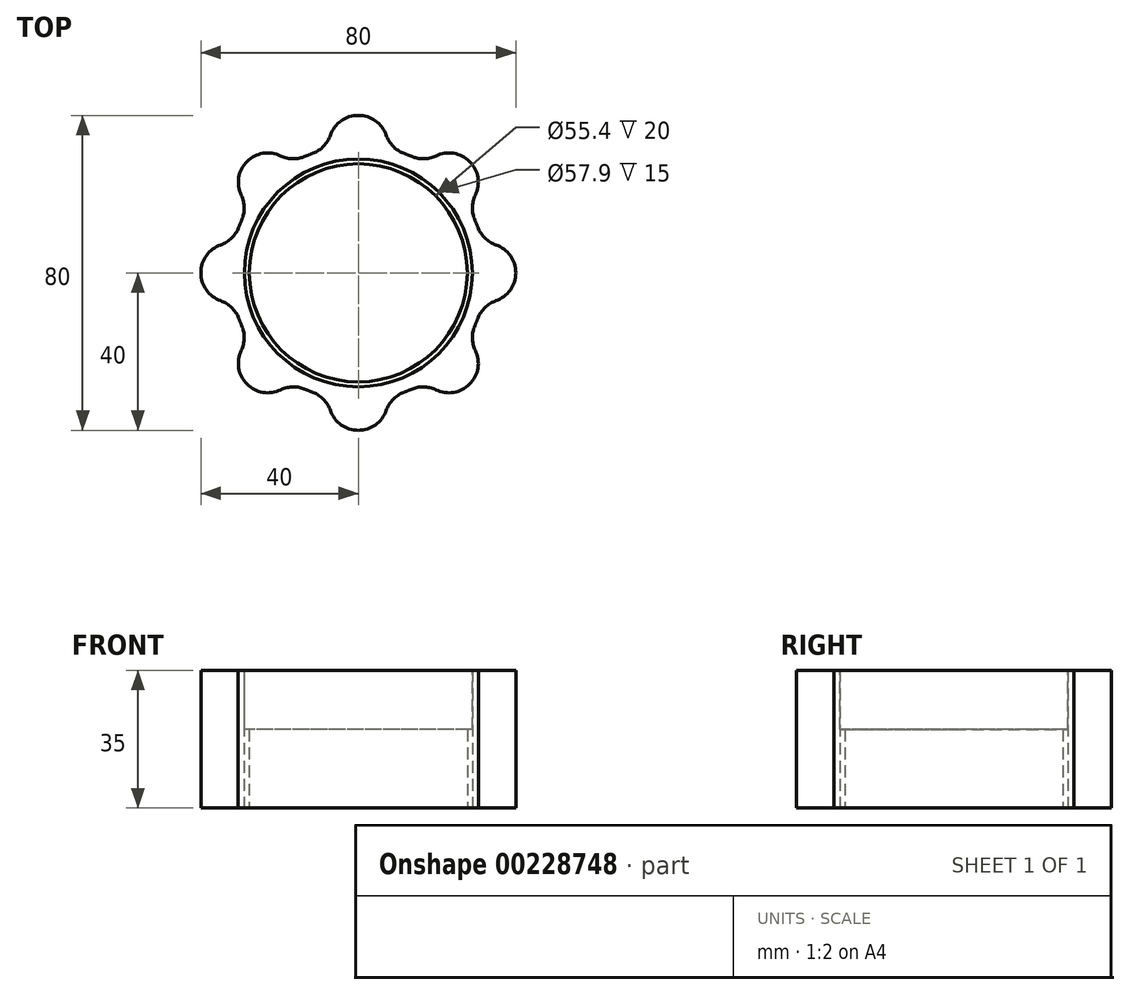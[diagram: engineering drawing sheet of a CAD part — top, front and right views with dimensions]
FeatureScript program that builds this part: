
annotation { "Feature Type Name" : "Feature", "Feature Type Description" : "" }
export const myFeature = defineFeature(function(context is Context, id is Id, definition is map)
    precondition{}
    {
        {
            var Q0;
            Q0=qCreatedBy(makeId("Top.planeOp"),FACE);
            var sketch = newSketch(context, id + "F0", { "sketchPlane" : qUnion([Q0])});
            skCircle(sketch, "E0", {"center": v(0, 0) * mm, "radius": 27.7 * mm});
            skCircle(sketch, "E1", {"center": v(0, 0) * mm, "radius": 40 * mm, "construction": true});
            skArc(sketch, "E2", {"start": v(-11.52, 30.4) * mm, "mid": v(-12.44, 30.03) * mm, "end": v(-13.35, 29.63) * mm});
            skArc(sketch, "E3", {"start": v(7.09, 34.95) * mm, "mid": v(0, 40) * mm, "end": v(-7.09, 34.95) * mm});
            skPoint(sketch, "E4.visualSharp", {"position": v(-7.45, 31.63) * mm});
            skArc(sketch, "E4.filletArc", {"start": v(-11.52, 30.4) * mm, "mid": v(-8.8, 32.18) * mm, "end": v(-7.09, 34.95) * mm});
            skPoint(sketch, "E5.visualSharp", {"position": v(7.45, 31.63) * mm});
            skArc(sketch, "E5.filletArc", {"start": v(7.09, 34.95) * mm, "mid": v(8.8, 32.18) * mm, "end": v(11.52, 30.4) * mm});
            skArc(sketch, "E6.1.0", {"start": v(-29.63, 13.35) * mm, "mid": v(-28.97, 16.53) * mm, "end": v(-29.73, 19.7) * mm});
            skArc(sketch, "E6.1.1", {"start": v(-19.7, 29.73) * mm, "mid": v(-28.28, 28.28) * mm, "end": v(-29.73, 19.7) * mm});
            skArc(sketch, "E6.1.2", {"start": v(-19.7, 29.73) * mm, "mid": v(-16.53, 28.97) * mm, "end": v(-13.35, 29.63) * mm});
            skArc(sketch, "E6.2.0", {"start": v(-30.4, -11.52) * mm, "mid": v(-32.18, -8.8) * mm, "end": v(-34.95, -7.09) * mm});
            skArc(sketch, "E6.2.1", {"start": v(-34.95, 7.09) * mm, "mid": v(-40, 0) * mm, "end": v(-34.95, -7.09) * mm});
            skArc(sketch, "E6.2.2", {"start": v(-34.95, 7.09) * mm, "mid": v(-32.18, 8.8) * mm, "end": v(-30.4, 11.52) * mm});
            skArc(sketch, "E6.3.0", {"start": v(-13.35, -29.63) * mm, "mid": v(-16.53, -28.97) * mm, "end": v(-19.7, -29.73) * mm});
            skArc(sketch, "E6.3.1", {"start": v(-29.73, -19.7) * mm, "mid": v(-28.28, -28.28) * mm, "end": v(-19.7, -29.73) * mm});
            skArc(sketch, "E6.3.2", {"start": v(-29.73, -19.7) * mm, "mid": v(-28.97, -16.53) * mm, "end": v(-29.63, -13.35) * mm});
            skArc(sketch, "E6.4.0", {"start": v(11.52, -30.4) * mm, "mid": v(8.8, -32.18) * mm, "end": v(7.09, -34.95) * mm});
            skArc(sketch, "E6.4.1", {"start": v(-7.09, -34.95) * mm, "mid": v(0, -40) * mm, "end": v(7.09, -34.95) * mm});
            skArc(sketch, "E6.4.2", {"start": v(-7.09, -34.95) * mm, "mid": v(-8.8, -32.18) * mm, "end": v(-11.52, -30.4) * mm});
            skArc(sketch, "E6.5.0", {"start": v(29.63, -13.35) * mm, "mid": v(28.97, -16.53) * mm, "end": v(29.73, -19.7) * mm});
            skArc(sketch, "E6.5.1", {"start": v(19.7, -29.73) * mm, "mid": v(28.28, -28.28) * mm, "end": v(29.73, -19.7) * mm});
            skArc(sketch, "E6.5.2", {"start": v(19.7, -29.73) * mm, "mid": v(16.53, -28.97) * mm, "end": v(13.35, -29.63) * mm});
            skArc(sketch, "E6.6.0", {"start": v(30.4, 11.52) * mm, "mid": v(32.18, 8.8) * mm, "end": v(34.95, 7.09) * mm});
            skArc(sketch, "E6.6.1", {"start": v(34.95, -7.09) * mm, "mid": v(40, 0) * mm, "end": v(34.95, 7.09) * mm});
            skArc(sketch, "E6.6.2", {"start": v(34.95, -7.09) * mm, "mid": v(32.18, -8.8) * mm, "end": v(30.4, -11.52) * mm});
            skArc(sketch, "E6.7.0", {"start": v(13.35, 29.63) * mm, "mid": v(16.53, 28.97) * mm, "end": v(19.7, 29.73) * mm});
            skArc(sketch, "E6.7.1", {"start": v(29.73, 19.7) * mm, "mid": v(28.28, 28.28) * mm, "end": v(19.7, 29.73) * mm});
            skArc(sketch, "E6.7.2", {"start": v(29.73, 19.7) * mm, "mid": v(28.97, 16.53) * mm, "end": v(29.63, 13.35) * mm});
            skArc(sketch, "E7.trimOffspring", {"start": v(-29.63, 13.35) * mm, "mid": v(-30.03, 12.44) * mm, "end": v(-30.4, 11.52) * mm});
            skArc(sketch, "E8.trimOffspring", {"start": v(-30.4, -11.52) * mm, "mid": v(-30.03, -12.44) * mm, "end": v(-29.63, -13.35) * mm});
            skArc(sketch, "E9.trimOffspring", {"start": v(-13.35, -29.63) * mm, "mid": v(-12.44, -30.03) * mm, "end": v(-11.52, -30.4) * mm});
            skArc(sketch, "E10.trimOffspring", {"start": v(11.52, -30.4) * mm, "mid": v(12.44, -30.03) * mm, "end": v(13.35, -29.63) * mm});
            skArc(sketch, "E11.trimOffspring", {"start": v(29.63, -13.35) * mm, "mid": v(30.03, -12.44) * mm, "end": v(30.4, -11.52) * mm});
            skArc(sketch, "E12.trimOffspring", {"start": v(30.4, 11.52) * mm, "mid": v(30.03, 12.44) * mm, "end": v(29.63, 13.35) * mm});
            skArc(sketch, "E13.trimOffspring", {"start": v(13.35, 29.63) * mm, "mid": v(12.44, 30.03) * mm, "end": v(11.52, 30.4) * mm});
            skSolve(sketch);
        }
        {
            var Q0;
            Q0=qSketchRegion(id+"F0",true);
            extrude(context, id + "F1", {"entities" : qUnion([Q0]), "depth" : 35 * mm});
        }
        {
            var Q0;
            Q0=makeQuery(id+"F1.opExtrude","CAP_FACE",FACE,{"disambiguationData":[OSD([sQuery(id+"F0.wireOp",EDGE,"E0"),sQuery(id+"F0.wireOp",EDGE,"E2"),sQuery(id+"F0.wireOp",EDGE,"E3"),sQuery(id+"F0.wireOp",EDGE,"E4.filletArc"),sQuery(id+"F0.wireOp",EDGE,"E5.filletArc"),sQuery(id+"F0.wireOp",EDGE,"E6.1.0"),sQuery(id+"F0.wireOp",EDGE,"E6.1.1"),sQuery(id+"F0.wireOp",EDGE,"E6.1.2"),sQuery(id+"F0.wireOp",EDGE,"E6.2.0"),sQuery(id+"F0.wireOp",EDGE,"E6.2.1"),sQuery(id+"F0.wireOp",EDGE,"E6.2.2"),sQuery(id+"F0.wireOp",EDGE,"E6.3.0"),sQuery(id+"F0.wireOp",EDGE,"E6.3.1"),sQuery(id+"F0.wireOp",EDGE,"E6.3.2"),sQuery(id+"F0.wireOp",EDGE,"E6.4.0"),sQuery(id+"F0.wireOp",EDGE,"E6.4.1"),sQuery(id+"F0.wireOp",EDGE,"E6.4.2"),sQuery(id+"F0.wireOp",EDGE,"E6.5.0"),sQuery(id+"F0.wireOp",EDGE,"E6.5.1"),sQuery(id+"F0.wireOp",EDGE,"E6.5.2"),sQuery(id+"F0.wireOp",EDGE,"E6.6.0"),sQuery(id+"F0.wireOp",EDGE,"E6.6.1"),sQuery(id+"F0.wireOp",EDGE,"E6.6.2"),sQuery(id+"F0.wireOp",EDGE,"E6.7.0"),sQuery(id+"F0.wireOp",EDGE,"E6.7.1"),sQuery(id+"F0.wireOp",EDGE,"E6.7.2"),sQuery(id+"F0.wireOp",EDGE,"E7.trimOffspring"),sQuery(id+"F0.wireOp",EDGE,"E8.trimOffspring"),sQuery(id+"F0.wireOp",EDGE,"E9.trimOffspring"),sQuery(id+"F0.wireOp",EDGE,"E10.trimOffspring"),sQuery(id+"F0.wireOp",EDGE,"E11.trimOffspring"),sQuery(id+"F0.wireOp",EDGE,"E12.trimOffspring"),sQuery(id+"F0.wireOp",EDGE,"E13.trimOffspring")])],"isStart":false});
            var sketch = newSketch(context, id + "F2", { "sketchPlane" : qUnion([Q0])});
            skCircle(sketch, "E14", {"center": v(0, 0) * mm, "radius": 28.95 * mm});
            skSolve(sketch);
        }
        {
            var Q0;
            Q0=qSketchRegion(id+"F2",true);
            extrude(context, id + "F3", {"entities" : qUnion([Q0]), "operationType" : NewBodyOperationType.REMOVE, "oppositeDirection" : true, "depth" : 15 * mm});
        }
    });
